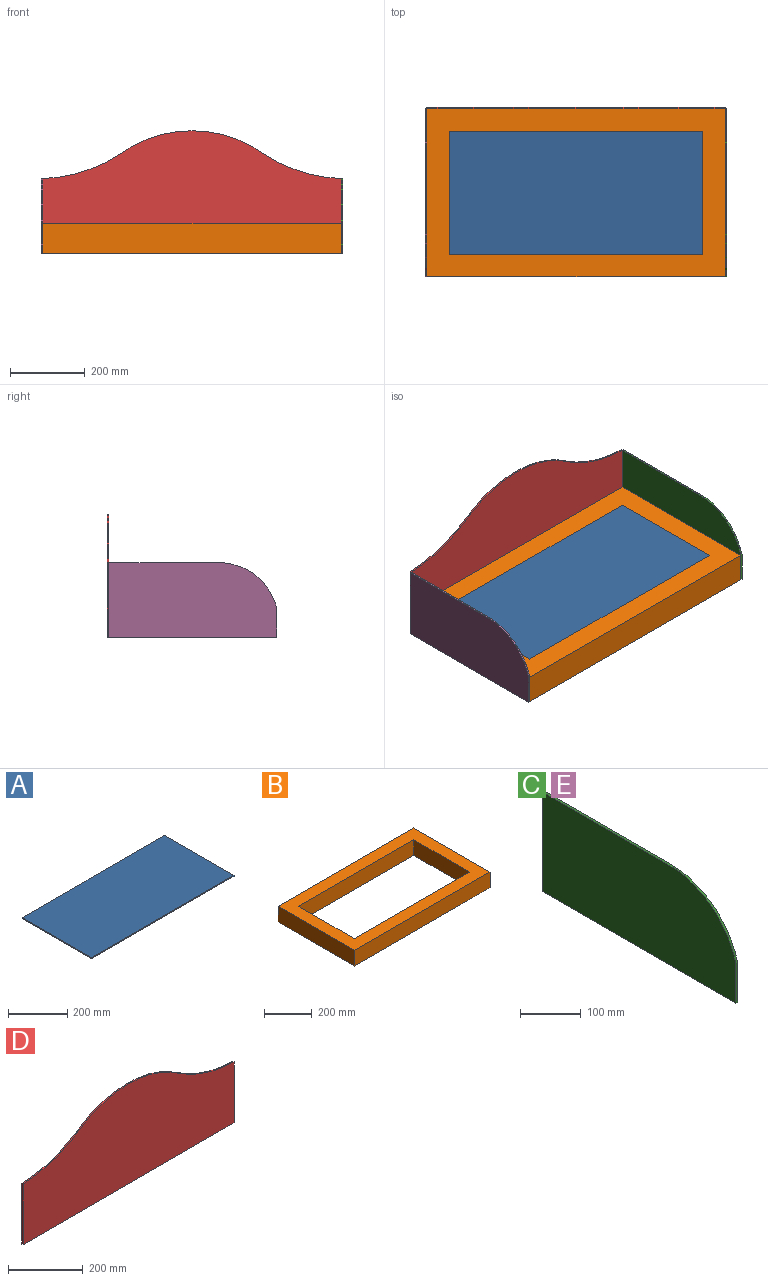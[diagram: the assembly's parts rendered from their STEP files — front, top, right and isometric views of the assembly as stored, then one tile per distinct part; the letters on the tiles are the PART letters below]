
ASSEMBLY  parts=5 mates=4
PART A: 6 faces, bbox 680x330x4 mm
  f0: plane 680x4mm, normal (0,-1,0), area 2720mm2, adj f1,f3,f4,f5
  f1: plane 330x4mm, normal (1,0,0), area 1320mm2, adj f0,f2,f4,f5
  f2: plane 680x4mm, normal (0,1,0), area 2720mm2, adj f1,f3,f4,f5
  f3: plane 330x4mm, normal (-1,0,0), area 1320mm2, adj f0,f2,f4,f5
  f4: plane 680x330mm, normal (0,0,1), area 224400mm2, adj f0,f1,f2,f3
  f5: plane 680x330mm, normal (0,0,-1), area 224400mm2, adj f0,f1,f2,f3
PART B: 10 faces, bbox 800x450x80 mm
  f0: plane 800x80mm, normal (0,-1,0), area 64000mm2, adj f1,f7,f8,f9
  f1: plane 450x80mm, normal (1,0,0), area 36000mm2, adj f0,f2,f8,f9
  f2: plane 800x80mm, normal (0,1,0), area 64000mm2, adj f1,f7,f8,f9
  f3: plane 330x80mm, normal (-1,0,0), area 26400mm2, adj f4,f6,f8,f9
  f4: plane 680x80mm, normal (0,1,0), area 54400mm2, adj f3,f5,f8,f9
  f5: plane 330x80mm, normal (1,0,0), area 26400mm2, adj f4,f6,f8,f9
  f6: plane 680x80mm, normal (0,-1,0), area 54400mm2, adj f3,f5,f8,f9
  f7: plane 450x80mm, normal (-1,0,0), area 36000mm2, adj f0,f2,f8,f9
  f8: plane 800x450mm, normal (0,0,1), area 135600mm2, adj f0,f1,f2,f3,f4,f5,f6,f7
  f9: plane 800x450mm, normal (0,0,-1), area 135600mm2, adj f0,f1,f2,f3,f4,f5,f6,f7
PART C: 7 faces, bbox 4x450x200 mm
  f0: plane 450x4mm, normal (0,0,-1), area 1800mm2, adj f1,f4,f5,f6
  f1: plane 200x4mm, normal (0,1,0), area 800mm2, adj f0,f2,f5,f6
  f2: plane 294.24x4mm, normal (0,0,1), area 1177mm2, adj f1,f3,f5,f6
  f3: cylinder r=161.08mm len=155.76mm, axis (-1,0,0), area 845.9mm2, adj f2,f4,f5,f6
  f4: plane 80x4mm, normal (0,-1,0), area 320mm2, adj f0,f3,f5,f6
  f5: plane 450x200mm, normal (1,0,0), area 85143.3mm2, adj f0,f1,f2,f3,f4
  f6: plane 450x200mm, normal (-1,0,0), area 85143.3mm2, adj f0,f1,f2,f3,f4
PART D: 8 faces, bbox 800x4x328.2 mm
  f0: plane 800x4mm, normal (0,0,-1), area 3200mm2, adj f1,f5,f6,f7
  f1: plane 200x4mm, normal (1,0,0), area 800mm2, adj f0,f2,f6,f7
  f2: cylinder r=397.76mm len=208.02mm, axis (0,1,0), area 885mm2, adj f1,f3,f6,f7
  f3: cylinder r=330mm len=383.97mm, axis (0,1,0), area 1639.2mm2, adj f2,f4,f6,f7
  f4: cylinder r=397.76mm len=208.02mm, axis (0,1,0), area 885mm2, adj f3,f5,f6,f7
  f5: plane 200x4mm, normal (-1,0,0), area 800mm2, adj f0,f4,f6,f7
  f6: plane 800x328.19mm, normal (0,-1,0), area 211042.1mm2, adj f0,f1,f2,f3,f4,f5
  f7: plane 800x328.19mm, normal (0,1,0), area 211042.1mm2, adj f0,f1,f2,f3,f4,f5
PART E: same geometry as C
PLACE A t=(872.3,109.12,-109.55)mm
PLACE B t=(872.3,109.12,-185.55)mm
PLACE C t=(1272.3,109.12,-85.55)mm
PLACE D t=(872.3,338.12,-85.55)mm
PLACE E t=(468.3,109.12,-85.55)mm
MATE fastened D.f6 <-> B.f2  axis (0,-1,0) through (872.3,334.12,-185.55)mm
MATE fastened E.f5 <-> B.f7  axis (1,0,0) through (472.3,109.12,-185.55)mm
MATE fastened C.f6 <-> B.f1  axis (-1,0,0) through (1272.3,109.12,-185.55)mm
MATE fastened B.f8 <-> A.f4  axis (0,0,1) through (872.3,-55.88,-105.55)mm
